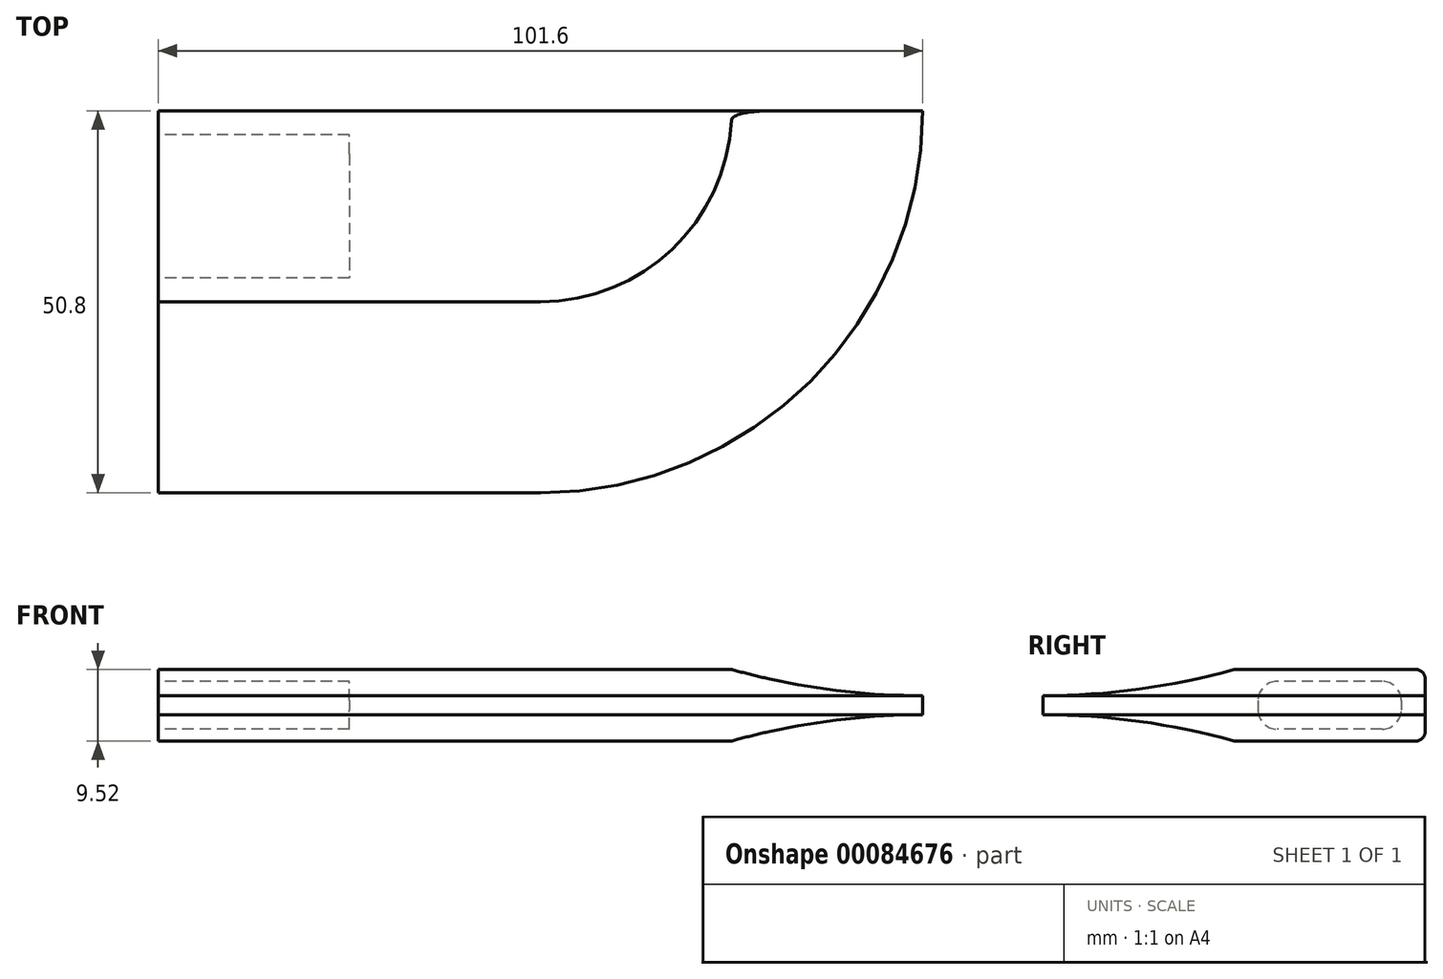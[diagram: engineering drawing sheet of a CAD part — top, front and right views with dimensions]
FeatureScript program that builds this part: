
annotation { "Feature Type Name" : "Feature", "Feature Type Description" : "" }
export const myFeature = defineFeature(function(context is Context, id is Id, definition is map)
    precondition{}
    {
        {
            var Q0;
            Q0=qCreatedBy(makeId("Top.planeOp"),FACE);
            var sketch = newSketch(context, id + "F0", { "sketchPlane" : qUnion([Q0])});
            skLineSegment(sketch, "E0", {"start": v(0, 0) * mm, "end": v(0, -50.8) * mm});
            skLineSegment(sketch, "E1", {"start": v(0, -50.8) * mm, "end": v(50.8, -50.8) * mm});
            skArc(sketch, "E2", {"start": v(50.8, -50.8) * mm, "mid": v(86.72, -35.92) * mm, "end": v(101.6, 0) * mm});
            skLineSegment(sketch, "E3", {"start": v(101.6, 0) * mm, "end": v(0, 0) * mm});
            skSolve(sketch);
        }
        {
            var Q0;
            Q0=makeQuery(id+"F0.imprint","IMPRINT",FACE,{"disambiguationData":[TD([[makeQuery(id+"F0.imprint","IMPRINT",EDGE,{"derivedFrom":sQuery(id+"F0.wireOp",EDGE,"E0")}),1.0]])]});
            extrude(context, id + "F1", {"entities" : qUnion([Q0]), "endBound" : BoundingType.SYMMETRIC, "depth" : 9.52 * mm});
        }
        {
            var Q0;
            Q0=makeQuery(id+"F1.opExtrude","SWEPT_FACE",FACE,{"disambiguationData":[OSD([sQuery(id+"F0.wireOp",EDGE,"E0")])]});
            var sketch = newSketch(context, id + "F2", { "sketchPlane" : qUnion([Q0])});
            skLineSegment(sketch, "E4.bottom", {"start": v(3.18, 3.17) * mm, "end": v(22.23, 3.17) * mm});
            skLineSegment(sketch, "E4.top", {"start": v(3.18, -3.18) * mm, "end": v(22.23, -3.18) * mm});
            skLineSegment(sketch, "E4.left", {"start": v(3.18, 3.17) * mm, "end": v(3.18, -3.18) * mm});
            skLineSegment(sketch, "E4.right", {"start": v(22.23, 3.17) * mm, "end": v(22.23, -3.17) * mm});
            skPoint(sketch, "E4.middle", {"position": v(12.7, 0) * mm});
            skSolve(sketch);
        }
        {
            var Q0;
            Q0 = qSketchRegion(id + "F2", true);
            extrude(context, id + "F3", {"entities" : qUnion([Q0]), "operationType" : NewBodyOperationType.REMOVE, "oppositeDirection" : true, "depth" : 25.4 * mm});
        }
        {
            var Q0;
            Q0=makeQuery(id+"F3.boolean.opBoolean","COPY",EDGE,{"derivedFrom":makeQuery(id+"F3.opExtrude","SWEPT_EDGE",EDGE,{"disambiguationData":[OSD([sQuery(id+"F2.wireOp",EDGE,"E4.bottom"),sQuery(id+"F2.wireOp",EDGE,"E4.left")])]})});
            var Q1;
            Q1=makeQuery(id+"F3.boolean.opBoolean","COPY",EDGE,{"derivedFrom":makeQuery(id+"F3.opExtrude","SWEPT_EDGE",EDGE,{"disambiguationData":[OSD([sQuery(id+"F2.wireOp",EDGE,"E4.bottom"),sQuery(id+"F2.wireOp",EDGE,"E4.right")])]})});
            var Q2;
            Q2=makeQuery(id+"F3.boolean.opBoolean","COPY",EDGE,{"derivedFrom":makeQuery(id+"F3.opExtrude","SWEPT_EDGE",EDGE,{"disambiguationData":[OSD([sQuery(id+"F2.wireOp",EDGE,"E4.top"),sQuery(id+"F2.wireOp",EDGE,"E4.left")])]})});
            var Q3;
            Q3=makeQuery(id+"F3.boolean.opBoolean","COPY",EDGE,{"derivedFrom":makeQuery(id+"F3.opExtrude","SWEPT_EDGE",EDGE,{"disambiguationData":[OSD([sQuery(id+"F2.wireOp",EDGE,"E4.top"),sQuery(id+"F2.wireOp",EDGE,"E4.right")])]})});
            fillet(context, id + "F4", {"entities" : qUnion([Q0, Q1, Q2, Q3]), "radius" : 2.54 * mm, "tangentPropagation" : true, "allowEdgeOverflow" : false});
        }
        {
            var Q0;
            Q0=makeQuery(id+"F1.opExtrude","SWEPT_FACE",FACE,{"disambiguationData":[OSD([sQuery(id+"F0.wireOp",EDGE,"E0")])]});
            var sketch = newSketch(context, id + "F5", { "sketchPlane" : qUnion([Q0])});
            skArc(sketch, "E5", {"start": v(25.4, 4.76) * mm, "mid": v(37.98, 2.15) * mm, "end": v(50.8, 1.27) * mm});
            skLineSegment(sketch, "E6", {"start": v(50.8, 1.27) * mm, "end": v(63.08, 1.27) * mm, "construction": true});
            skLineSegment(sketch, "E7", {"start": v(25.4, 4.76) * mm, "end": v(50.8, 4.76) * mm});
            skLineSegment(sketch, "E8", {"start": v(50.8, 4.76) * mm, "end": v(50.8, 1.27) * mm});
            skSolve(sketch);
        }
        {
            var Q0;
            Q0 = qSketchRegion(id + "F5", true);
            var Q1;
            Q1=makeQuery(id+"F1.opExtrude","CAP_EDGE",EDGE,{"disambiguationData":[OSD([sQuery(id+"F0.wireOp",EDGE,"E1")])],"isStart":false});
            var Q2;
            Q2=makeQuery(id+"F1.opExtrude","CAP_EDGE",EDGE,{"disambiguationData":[OSD([sQuery(id+"F0.wireOp",EDGE,"E2")])],"isStart":false});
            sweep(context, id + "F6", {"profiles" : qUnion([Q0]), "path" : qUnion([Q1, Q2])});
        }
        {
            var Q0;
            Q0=makeQuery(id+"F6.opSweep","SWEPT_BODY",BODY,{"disambiguationData":[OSD([sQuery(id+"F0.wireOp",EDGE,"E2"),sQuery(id+"F5.wireOp",EDGE,"E5"),sQuery(id+"F5.wireOp",EDGE,"E7"),sQuery(id+"F5.wireOp",EDGE,"E8")])]});
            var Q1;
            Q1=qCreatedBy(makeId("Top.planeOp"),FACE);
            mirror(context, id + "F7", {"entities" : qUnion([Q0]), "mirrorPlane" : qUnion([Q1])});
        }
        {
            var Q0;
            Q0=makeQuery(id+"F6.opSweep","SWEPT_BODY",BODY,{"disambiguationData":[OSD([sQuery(id+"F0.wireOp",EDGE,"E2"),sQuery(id+"F5.wireOp",EDGE,"E5"),sQuery(id+"F5.wireOp",EDGE,"E7"),sQuery(id+"F5.wireOp",EDGE,"E8")])]});
            var Q1;
            Q1=makeQuery(id+"F7.opPattern","COPY",BODY,{"derivedFrom":makeQuery(id+"F6.opSweep","SWEPT_BODY",BODY,{"disambiguationData":[OSD([sQuery(id+"F0.wireOp",EDGE,"E2"),sQuery(id+"F5.wireOp",EDGE,"E5"),sQuery(id+"F5.wireOp",EDGE,"E7"),sQuery(id+"F5.wireOp",EDGE,"E8")])]}),"instanceName":"1"});
            var Q2;
            Q2=makeQuery(id+"F1.opExtrude","SWEPT_BODY",BODY,{"disambiguationData":[OSD([sQuery(id+"F0.wireOp",EDGE,"E0"),sQuery(id+"F0.wireOp",EDGE,"E1"),sQuery(id+"F0.wireOp",EDGE,"E2"),sQuery(id+"F0.wireOp",EDGE,"E3")])]});
            booleanBodies(context, id + "F8", {"operationType" : BooleanOperationType.SUBTRACTION, "tools" : qUnion([Q0, Q1]), "targets" : qUnion([Q2])});
        }
        {
            var Q0;
            Q0=makeQuery(id+"F8.opBoolean","COPY",EDGE,{"derivedFrom":makeQuery(id+"F6.opSweep","SWEPT_EDGE",EDGE,{"disambiguationData":[OSD([sQuery(id+"F0.wireOp",EDGE,"E0"),sQuery(id+"F0.wireOp",EDGE,"E1"),sQuery(id+"F5.wireOp",EDGE,"E5"),sQuery(id+"F5.wireOp",EDGE,"E8")])]})});
            var Q1;
            Q1=makeQuery(id+"F8.opBoolean","COPY",EDGE,{"derivedFrom":makeQuery(id+"F7.opPattern","COPY",EDGE,{"derivedFrom":makeQuery(id+"F6.opSweep","SWEPT_EDGE",EDGE,{"disambiguationData":[OSD([sQuery(id+"F0.wireOp",EDGE,"E0"),sQuery(id+"F0.wireOp",EDGE,"E1"),sQuery(id+"F5.wireOp",EDGE,"E5"),sQuery(id+"F5.wireOp",EDGE,"E8")])]}),"instanceName":"1"})});
            var Q2;
            Q2=makeQuery(id+"F8.opBoolean","COPY",EDGE,{"derivedFrom":makeQuery(id+"F6.opSweep","CAP_EDGE",EDGE,{"disambiguationData":[OSD([sQuery(id+"F0.wireOp",EDGE,"E2"),sQuery(id+"F0.wireOp",EDGE,"E3"),sQuery(id+"F5.wireOp",EDGE,"E5")])],"isStart":false})});
            var Q3;
            Q3=makeQuery(id+"F8.opBoolean","COPY",EDGE,{"derivedFrom":makeQuery(id+"F7.opPattern","COPY",EDGE,{"derivedFrom":makeQuery(id+"F6.opSweep","CAP_EDGE",EDGE,{"disambiguationData":[OSD([sQuery(id+"F0.wireOp",EDGE,"E2"),sQuery(id+"F0.wireOp",EDGE,"E3"),sQuery(id+"F5.wireOp",EDGE,"E5")])],"isStart":false}),"instanceName":"1"})});
            var Q4;
            Q4=makeQuery(id+"F1.opExtrude","CAP_EDGE",EDGE,{"disambiguationData":[OSD([sQuery(id+"F0.wireOp",EDGE,"E3")])],"isStart":false});
            var Q5;
            Q5=makeQuery(id+"F1.opExtrude","CAP_EDGE",EDGE,{"disambiguationData":[OSD([sQuery(id+"F0.wireOp",EDGE,"E3")])],"isStart":true});
            fillet(context, id + "F9", {"entities" : qUnion([Q0, Q1, Q2, Q3, Q4, Q5]), "radius" : 1.27 * mm, "tangentPropagation" : true, "allowEdgeOverflow" : false});
        }
    });
